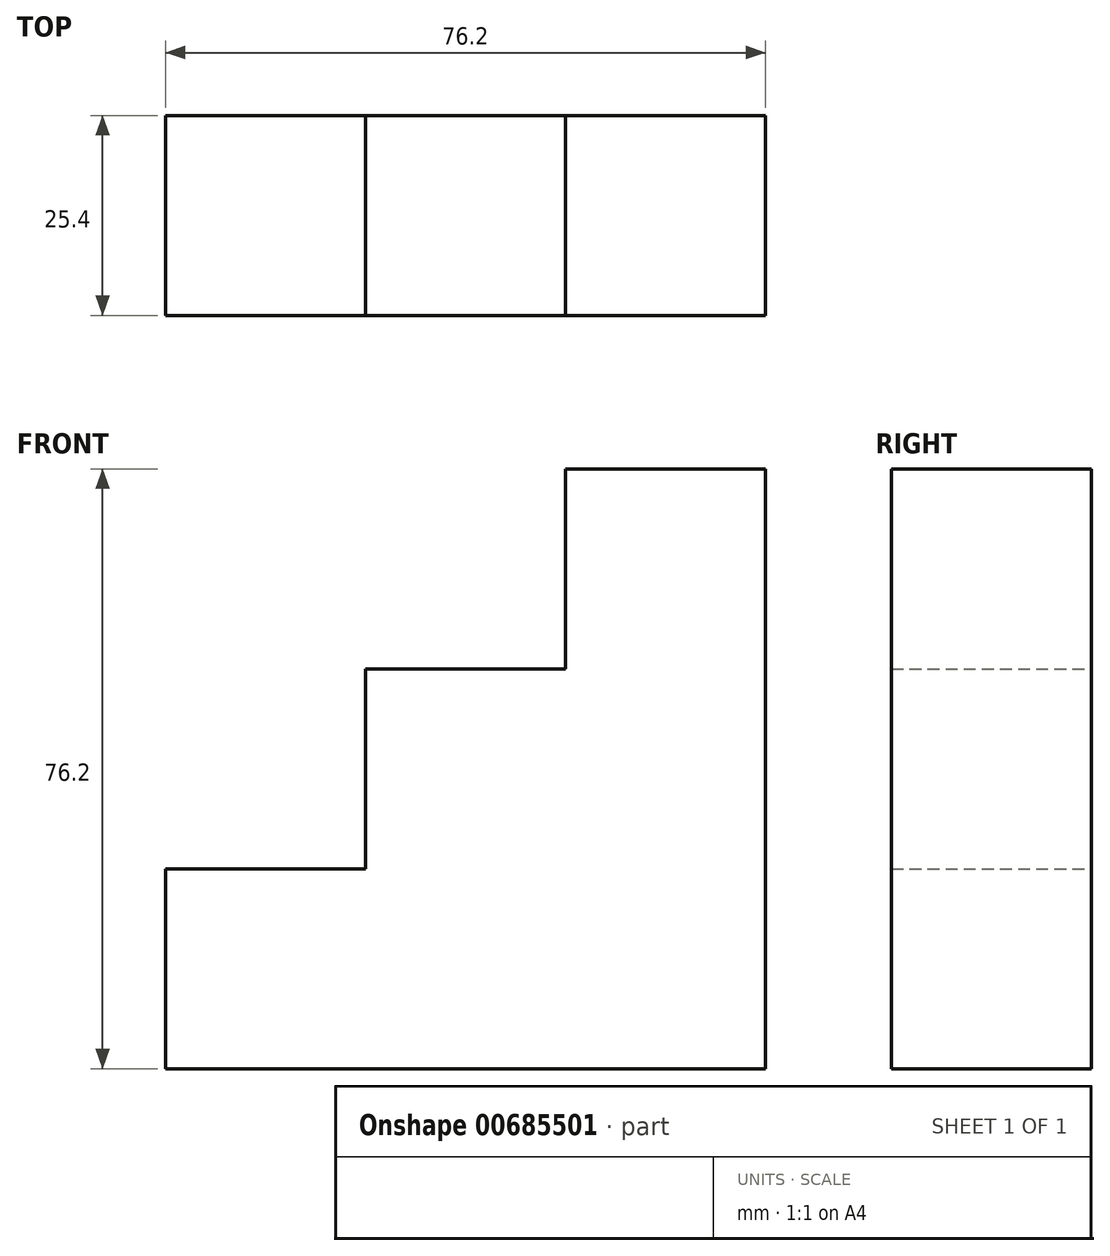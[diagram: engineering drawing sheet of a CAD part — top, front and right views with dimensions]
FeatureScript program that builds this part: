
annotation { "Feature Type Name" : "Feature", "Feature Type Description" : "" }
export const myFeature = defineFeature(function(context is Context, id is Id, definition is map)
    precondition{}
    {
        {
            var Q0;
            Q0=qCreatedBy(makeId("Front.planeOp"),FACE);
            var sketch = newSketch(context, id + "F0", { "sketchPlane" : qUnion([Q0])});
            skLineSegment(sketch, "E0", {"start": v(-25.4, -25.4) * mm, "end": v(50.8, -25.4) * mm});
            skLineSegment(sketch, "E1", {"start": v(50.8, -25.4) * mm, "end": v(50.8, 50.8) * mm});
            skLineSegment(sketch, "E2", {"start": v(50.8, 50.8) * mm, "end": v(25.4, 50.8) * mm});
            skLineSegment(sketch, "E3", {"start": v(25.4, 50.8) * mm, "end": v(25.4, 25.4) * mm});
            skLineSegment(sketch, "E4", {"start": v(25.4, 25.4) * mm, "end": v(0, 25.4) * mm});
            skLineSegment(sketch, "E5", {"start": v(0, 25.4) * mm, "end": v(0, 0) * mm});
            skLineSegment(sketch, "E6", {"start": v(0, 0) * mm, "end": v(-25.4, 0) * mm});
            skLineSegment(sketch, "E7", {"start": v(-25.4, 0) * mm, "end": v(-25.4, -25.4) * mm});
            skSolve(sketch);
        }
        {
            var Q0;
            Q0 = qSketchRegion(id + "F0", true);
            extrude(context, id + "F1", {"entities" : qUnion([Q0]), "depth" : 25.4 * mm, "offsetDistance" : 25.4 * mm});
        }
    });
